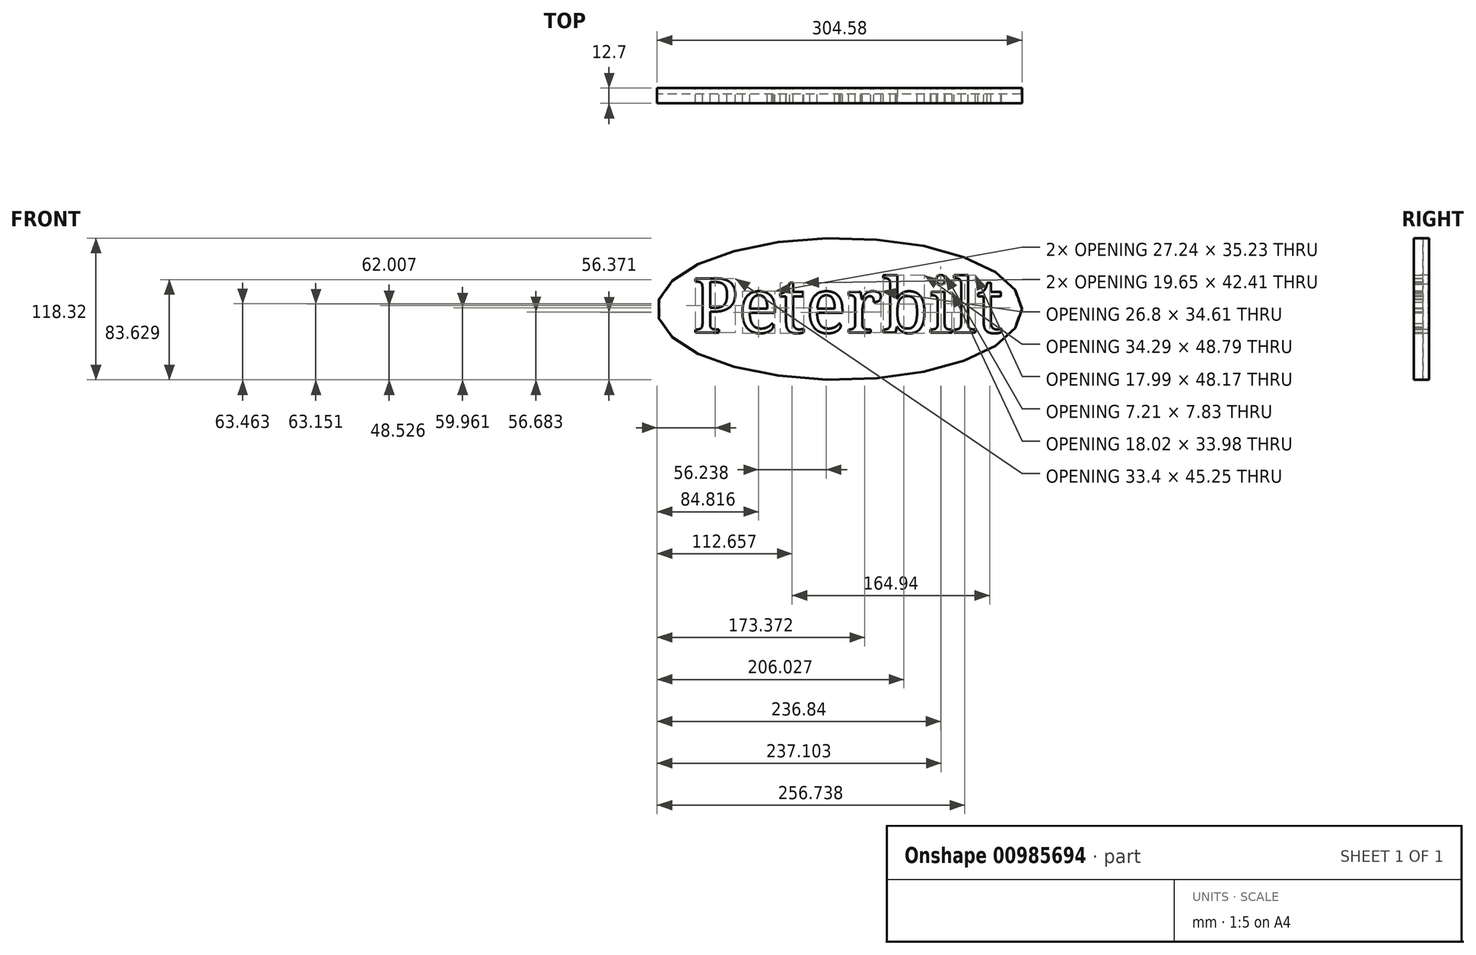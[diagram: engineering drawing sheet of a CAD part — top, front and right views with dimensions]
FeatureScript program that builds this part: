
annotation { "Feature Type Name" : "Feature", "Feature Type Description" : "" }
export const myFeature = defineFeature(function(context is Context, id is Id, definition is map)
    precondition{}
    {
        {
            var Q0;
            Q0=qCreatedBy(makeId("Front.planeOp"),FACE);
            var sketch = newSketch(context, id + "F0", { "sketchPlane" : qUnion([Q0])});
            skEllipse(sketch, "E0", {"center": v(0, 0) * mm, "majorRadius": 152.29 * mm, "minorRadius": 59.16 * mm, "majorAxis": v(1, 0)});
            skText(sketch, "E1", { "text": "Peterbilt", "fontName": "NotoSerif-Regular.ttf"});
            const initialGuessF0  = {"E1": [-0.12288, -0.01978, 1, 0, 0.04564]};
            skSetInitialGuess(sketch, initialGuessF0);
            skSolve(sketch);
        }
        {
            var Q0;
            Q0=makeQuery(id+"F0.imprint","IMPRINT",FACE,{"disambiguationData":[TD([[makeQuery(id+"F0.imprint","IMPRINT",EDGE,{"derivedFrom":sQuery(id+"F0.wireOp",EDGE,"E0")}),1.0]])]});
            extrude(context, id + "F1", {"entities" : qUnion([Q0]), "depth" : 12.7 * mm, "offsetDistance" : 25.4 * mm});
        }
        {
            var Q0;
            Q0=makeQuery(id+"F0.imprint","IMPRINT",FACE,{"disambiguationData":[TD([[makeQuery(id+"F0.imprint","IMPRINT",EDGE,{"derivedFrom":sQuery(id+"F0.wireOp",EDGE,"E1.sketch_text.stroke-214")}),1.0]])]});
            extrude(context, id + "F2", {"entities" : qUnion([Q0]), "depth" : 12.7 * mm, "offsetDistance" : 25.4 * mm});
        }
        {
            var Q0;
            Q0=makeQuery(id+"F0.imprint","IMPRINT",FACE,{"disambiguationData":[TD([[makeQuery(id+"F0.imprint","IMPRINT",EDGE,{"derivedFrom":sQuery(id+"F0.wireOp",EDGE,"E1.sketch_text.stroke-101")}),1.0]])]});
            extrude(context, id + "F3", {"entities" : qUnion([Q0]), "depth" : 12.7 * mm, "offsetDistance" : 25.4 * mm});
        }
        {
            var Q0;
            Q0=makeQuery(id+"F0.imprint","IMPRINT",FACE,{"disambiguationData":[TD([[makeQuery(id+"F0.imprint","IMPRINT",EDGE,{"derivedFrom":sQuery(id+"F0.wireOp",EDGE,"E1.sketch_text.stroke-42")}),1.0]])]});
            extrude(context, id + "F4", {"entities" : qUnion([Q0]), "depth" : 12.7 * mm, "offsetDistance" : 25.4 * mm});
        }
        {
            var Q0;
            Q0=makeQuery(id+"F0.imprint","IMPRINT",FACE,{"disambiguationData":[TD([[makeQuery(id+"F0.imprint","IMPRINT",EDGE,{"derivedFrom":sQuery(id+"F0.wireOp",EDGE,"E1.sketch_text.stroke-31")}),1.0]])]});
            extrude(context, id + "F5", {"entities" : qUnion([Q0]), "depth" : 12.7 * mm, "offsetDistance" : 25.4 * mm});
        }
        {
            var Q0;
            Q0=qCreatedBy(makeId("Front.planeOp"),FACE);
            var sketch = newSketch(context, id + "F6", { "sketchPlane" : qUnion([Q0])});
            skEllipse(sketch, "E2", {"center": v(0, 0) * mm, "majorRadius": 151.62 * mm, "minorRadius": 59.1 * mm, "majorAxis": v(1, 0)});
            skSolve(sketch);
        }
        {
            var Q0;
            Q0 = qSketchRegion(id + "F6", true);
            extrude(context, id + "F7", {"entities" : qUnion([Q0]), "depth" : 5.08 * mm, "offsetDistance" : 25.4 * mm});
        }
    });
